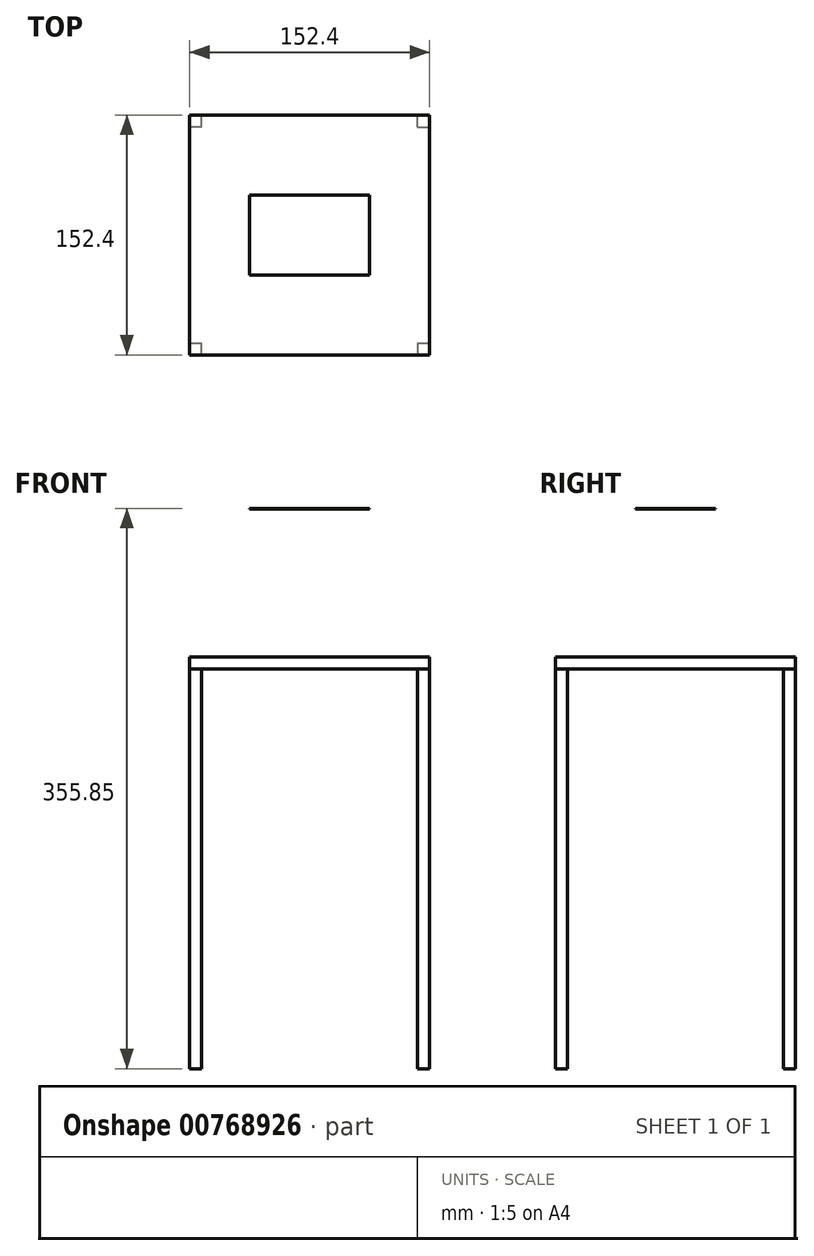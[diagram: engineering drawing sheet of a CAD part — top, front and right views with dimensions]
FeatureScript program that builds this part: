
annotation { "Feature Type Name" : "Feature", "Feature Type Description" : "" }
export const myFeature = defineFeature(function(context is Context, id is Id, definition is map)
    precondition{}
    {
        {
            var Q0;
            Q0=qCreatedBy(makeId("Top.planeOp"),FACE);
            var sketch = newSketch(context, id + "F0", { "sketchPlane" : qUnion([Q0])});
            skLineSegment(sketch, "E0.bottom", {"start": v(-76.2, -76.2) * mm, "end": v(76.2, -76.2) * mm});
            skLineSegment(sketch, "E0.top", {"start": v(-76.2, 76.2) * mm, "end": v(76.2, 76.2) * mm});
            skLineSegment(sketch, "E0.left", {"start": v(-76.2, -76.2) * mm, "end": v(-76.2, 76.2) * mm});
            skLineSegment(sketch, "E0.right", {"start": v(76.2, -76.2) * mm, "end": v(76.2, 76.2) * mm});
            skSolve(sketch);
        }
        {
            var Q0;
            Q0=makeQuery(id+"F0.imprint","IMPRINT",FACE,{"disambiguationData":[TD([[makeQuery(id+"F0.imprint","IMPRINT",EDGE,{"derivedFrom":sQuery(id+"F0.wireOp",EDGE,"E0.bottom")}),1.0]])]});
            var sketch = newSketch(context, id + "F1", { "sketchPlane" : qUnion([Q0])});
            skLineSegment(sketch, "E1.bottom", {"start": v(-76.2, -76.2) * mm, "end": v(-68.58, -76.2) * mm});
            skLineSegment(sketch, "E1.top", {"start": v(-76.2, -68.58) * mm, "end": v(-68.58, -68.58) * mm});
            skLineSegment(sketch, "E1.left", {"start": v(-76.2, -76.2) * mm, "end": v(-76.2, -68.58) * mm});
            skLineSegment(sketch, "E1.right", {"start": v(-68.58, -76.2) * mm, "end": v(-68.58, -68.58) * mm});
            skLineSegment(sketch, "E2.bottom", {"start": v(68.58, -68.58) * mm, "end": v(76.2, -68.58) * mm});
            skLineSegment(sketch, "E2.top", {"start": v(68.58, -76.2) * mm, "end": v(76.2, -76.2) * mm});
            skLineSegment(sketch, "E2.left", {"start": v(68.58, -68.58) * mm, "end": v(68.58, -76.2) * mm});
            skLineSegment(sketch, "E2.right", {"start": v(76.2, -68.58) * mm, "end": v(76.2, -76.2) * mm});
            skPoint(sketch, "E2.middle", {"position": v(72.4, -72.4) * mm});
            skLineSegment(sketch, "E3.bottom", {"start": v(68.58, 68.58) * mm, "end": v(76.2, 68.58) * mm});
            skLineSegment(sketch, "E3.top", {"start": v(68.58, 76.2) * mm, "end": v(76.2, 76.2) * mm});
            skLineSegment(sketch, "E3.left", {"start": v(68.58, 68.58) * mm, "end": v(68.58, 76.2) * mm});
            skLineSegment(sketch, "E3.right", {"start": v(76.2, 68.58) * mm, "end": v(76.2, 76.2) * mm});
            skPoint(sketch, "E3.middle", {"position": v(72.4, 72.4) * mm});
            skLineSegment(sketch, "E4.bottom", {"start": v(-68.58, 68.58) * mm, "end": v(-76.2, 68.58) * mm});
            skLineSegment(sketch, "E4.top", {"start": v(-68.58, 76.2) * mm, "end": v(-76.2, 76.2) * mm});
            skLineSegment(sketch, "E4.left", {"start": v(-68.58, 68.58) * mm, "end": v(-68.58, 76.2) * mm});
            skLineSegment(sketch, "E4.right", {"start": v(-76.2, 68.58) * mm, "end": v(-76.2, 76.2) * mm});
            skPoint(sketch, "E4.middle", {"position": v(-72.4, 72.4) * mm});
            skSolve(sketch);
        }
        {
            var Q0;
            Q0 = qSketchRegion(id + "F1", true);
            extrude(context, id + "F2", {"entities" : qUnion([Q0]), "oppositeDirection" : true, "depth" : 254 * mm, "offsetDistance" : 25.4 * mm});
        }
        {
            var Q0;
            Q0 = qSketchRegion(id + "F0", true);
            var Q1;
            Q1 = qConstructionFilter(qBodyType(qCreatedBy(id + "F0" ,EDGE), BodyType.WIRE), ConstructionObject.NO);
            extrude(context, id + "F3", {"entities" : qUnion([Q0]), "surfaceEntities" : qUnion([Q1]), "depth" : 7.62 * mm, "offsetDistance" : 25.4 * mm});
        }
        {
            var Q0;
            Q0=qCreatedBy(makeId("Top.planeOp"),FACE);
            cPlane(context, id + "F4", {"entities" : qUnion([Q0]), "cplaneType" : CPlaneType.OFFSET, "offset" : 101.6 * mm, "width" : 152.4 * mm, "height" : 152.4 * mm});
        }
        {
            var Q0;
            Q0=qCreatedBy(id+"F4.planeOp",FACE);
            var sketch = newSketch(context, id + "F5", { "sketchPlane" : qUnion([Q0])});
            skLineSegment(sketch, "E5.bottom", {"start": v(38.1, -25.4) * mm, "end": v(-38.1, -25.4) * mm});
            skLineSegment(sketch, "E5.top", {"start": v(38.1, 25.4) * mm, "end": v(-38.1, 25.4) * mm});
            skLineSegment(sketch, "E5.left", {"start": v(38.1, -25.4) * mm, "end": v(38.1, 25.4) * mm});
            skLineSegment(sketch, "E5.right", {"start": v(-38.1, -25.4) * mm, "end": v(-38.1, 25.4) * mm});
            skPoint(sketch, "E5.middle", {"position": v(0, 0) * mm});
            skSolve(sketch);
        }
        {
            var Q0;
            Q0=makeQuery(id+"F5.imprint","IMPRINT",FACE,{"disambiguationData":[TD([[makeQuery(id+"F5.imprint","IMPRINT",EDGE,{"derivedFrom":sQuery(id+"F5.wireOp",EDGE,"E5.bottom")}),-1.0]])]});
            extrude(context, id + "F6", {"entities" : qUnion([Q0]), "depth" : 0.25 * mm, "offsetDistance" : 25.4 * mm});
        }
    });
